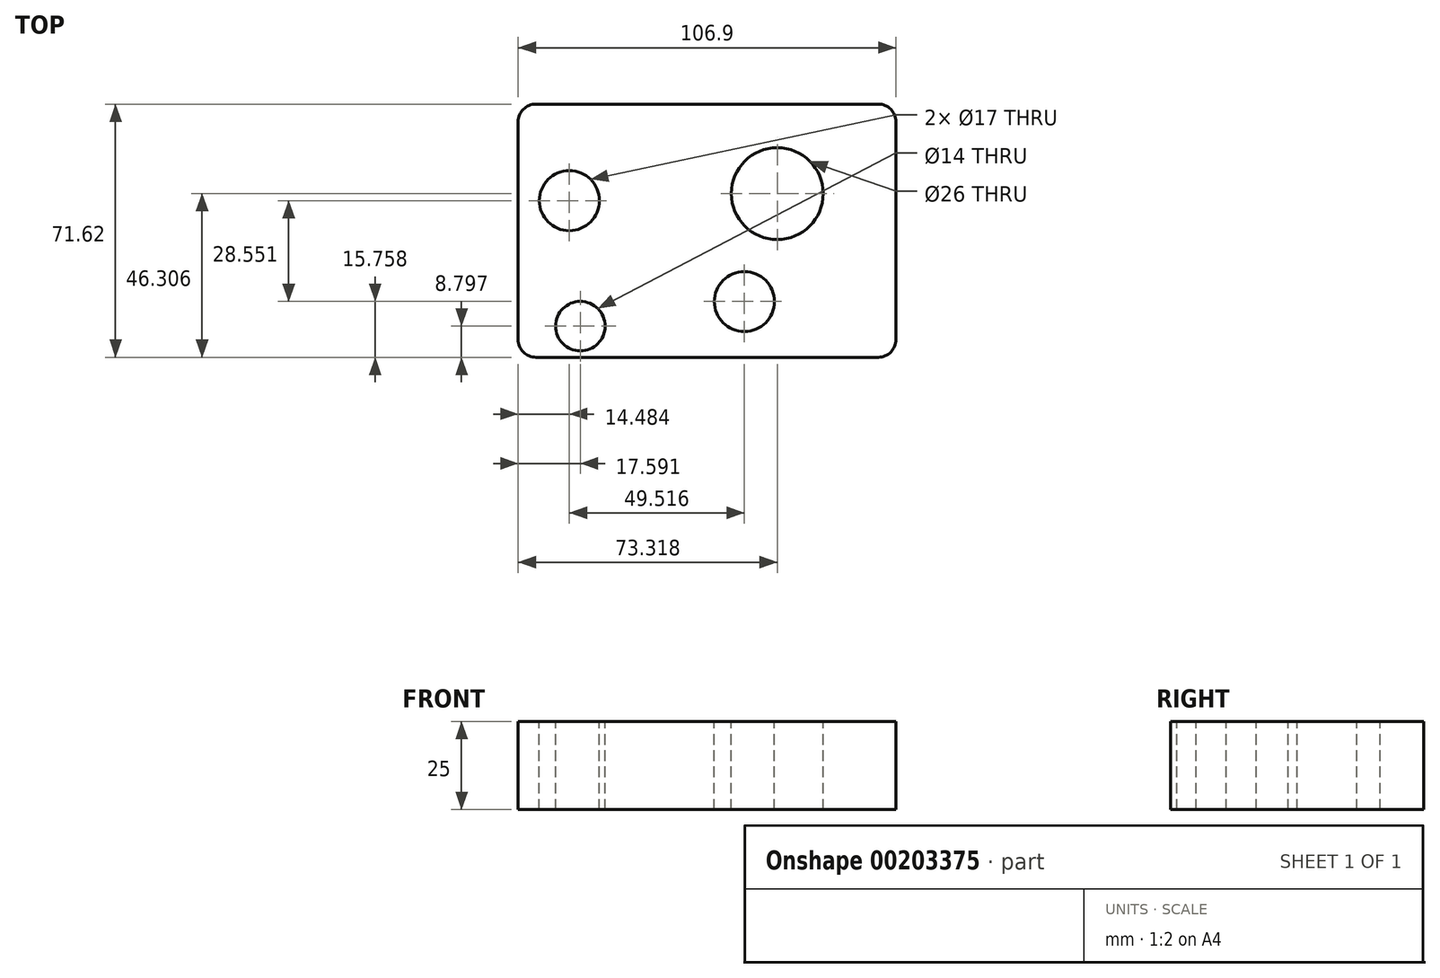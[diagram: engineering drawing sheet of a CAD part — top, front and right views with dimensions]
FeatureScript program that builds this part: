
annotation { "Feature Type Name" : "Feature", "Feature Type Description" : "" }
export const myFeature = defineFeature(function(context is Context, id is Id, definition is map)
    precondition{}
    {
        {
            var Q0;
            Q0=qCreatedBy(makeId("Top.planeOp"),FACE);
            var sketch = newSketch(context, id + "F0", { "sketchPlane" : qUnion([Q0])});
            skLineSegment(sketch, "E0.bottom", {"start": v(-45.31, 0) * mm, "end": v(61.6, 0) * mm});
            skLineSegment(sketch, "E0.top", {"start": v(-45.31, -71.62) * mm, "end": v(61.6, -71.62) * mm});
            skLineSegment(sketch, "E0.left", {"start": v(-45.31, 0) * mm, "end": v(-45.31, -71.62) * mm});
            skLineSegment(sketch, "E0.right", {"start": v(61.6, 0) * mm, "end": v(61.6, -71.62) * mm});
            skSolve(sketch);
        }
        {
            var Q0;
            Q0 = qSketchRegion(id + "F0", true);
            extrude(context, id + "F1", {"entities" : qUnion([Q0]), "depth" : 25 * mm});
        }
        {
            var Q0;
            Q0=makeQuery(id+"F1.opExtrude","SWEPT_EDGE",EDGE,{"disambiguationData":[OSD([sQuery(id+"F0.wireOp",EDGE,"E0.top"),sQuery(id+"F0.wireOp",EDGE,"E0.left")])]});
            var Q1;
            Q1=makeQuery(id+"F1.opExtrude","SWEPT_EDGE",EDGE,{"disambiguationData":[OSD([sQuery(id+"F0.wireOp",EDGE,"E0.top"),sQuery(id+"F0.wireOp",EDGE,"E0.right")])]});
            var Q2;
            Q2=makeQuery(id+"F1.opExtrude","SWEPT_EDGE",EDGE,{"disambiguationData":[OSD([sQuery(id+"F0.wireOp",EDGE,"E0.bottom"),sQuery(id+"F0.wireOp",EDGE,"E0.right")])]});
            var Q3;
            Q3=makeQuery(id+"F1.opExtrude","SWEPT_EDGE",EDGE,{"disambiguationData":[OSD([sQuery(id+"F0.wireOp",EDGE,"E0.bottom"),sQuery(id+"F0.wireOp",EDGE,"E0.left")])]});
            fillet(context, id + "F2", {"entities" : qUnion([Q0, Q1, Q2, Q3]), "radius" : 5 * mm, "tangentPropagation" : true, "allowEdgeOverflow" : false});
        }
        {
            var Q0;
            Q0=makeQuery(id+"F1.opExtrude","CAP_FACE",FACE,{"disambiguationData":[OSD([sQuery(id+"F0.wireOp",EDGE,"E0.bottom"),sQuery(id+"F0.wireOp",EDGE,"E0.top"),sQuery(id+"F0.wireOp",EDGE,"E0.left"),sQuery(id+"F0.wireOp",EDGE,"E0.right")])],"isStart":false});
            var sketch = newSketch(context, id + "F3", { "sketchPlane" : qUnion([Q0])});
            skCircle(sketch, "E1", {"center": v(-27.72, -62.82) * mm, "radius": 7.33 * mm});
            skCircle(sketch, "E2", {"center": v(-30.83, -27.31) * mm, "radius": 8.94 * mm});
            skCircle(sketch, "E3", {"center": v(18.7, -55.86) * mm, "radius": 8.77 * mm});
            skCircle(sketch, "E4", {"center": v(28, -25.31) * mm, "radius": 13.48 * mm});
            skSolve(sketch);
        }
        {
            var Q0;
            Q0=sQuery(id+"F3.wireOp",VERTEX,"E1.center");
            var Q1;
            Q1=makeQuery(id+"F1.opExtrude","SWEPT_BODY",BODY,{"disambiguationData":[OSD([sQuery(id+"F0.wireOp",EDGE,"E0.bottom"),sQuery(id+"F0.wireOp",EDGE,"E0.top"),sQuery(id+"F0.wireOp",EDGE,"E0.left"),sQuery(id+"F0.wireOp",EDGE,"E0.right")])]});
            hole(context, id + "F4", {"style" : HoleStyle.SIMPLE, "endStyle" : HoleEndStyle.THROUGH, "holeDiameter" : 14 * mm, "locations" : qUnion([Q0]), "scope" : qUnion([Q1]), "isTappedThrough" : true});
        }
        {
            var Q0;
            Q0=sQuery(id+"F3.wireOp",VERTEX,"E2.center");
            var Q1;
            Q1=makeQuery(id+"F1.opExtrude","SWEPT_BODY",BODY,{"disambiguationData":[OSD([sQuery(id+"F0.wireOp",EDGE,"E0.bottom"),sQuery(id+"F0.wireOp",EDGE,"E0.top"),sQuery(id+"F0.wireOp",EDGE,"E0.left"),sQuery(id+"F0.wireOp",EDGE,"E0.right")])]});
            hole(context, id + "F5", {"style" : HoleStyle.SIMPLE, "endStyle" : HoleEndStyle.THROUGH, "holeDiameter" : 17 * mm, "locations" : qUnion([Q0]), "scope" : qUnion([Q1]), "isTappedThrough" : true});
        }
        {
            var Q0;
            Q0=sQuery(id+"F3.wireOp",VERTEX,"E3.center");
            var Q1;
            Q1=makeQuery(id+"F1.opExtrude","SWEPT_BODY",BODY,{"disambiguationData":[OSD([sQuery(id+"F0.wireOp",EDGE,"E0.bottom"),sQuery(id+"F0.wireOp",EDGE,"E0.top"),sQuery(id+"F0.wireOp",EDGE,"E0.left"),sQuery(id+"F0.wireOp",EDGE,"E0.right")])]});
            hole(context, id + "F6", {"style" : HoleStyle.SIMPLE, "endStyle" : HoleEndStyle.THROUGH, "holeDiameter" : 17 * mm, "locations" : qUnion([Q0]), "scope" : qUnion([Q1]), "isTappedThrough" : true});
        }
        {
            var Q0;
            Q0=sQuery(id+"F3.wireOp",VERTEX,"E4.center");
            var Q1;
            Q1=makeQuery(id+"F1.opExtrude","SWEPT_BODY",BODY,{"disambiguationData":[OSD([sQuery(id+"F0.wireOp",EDGE,"E0.bottom"),sQuery(id+"F0.wireOp",EDGE,"E0.top"),sQuery(id+"F0.wireOp",EDGE,"E0.left"),sQuery(id+"F0.wireOp",EDGE,"E0.right")])]});
            hole(context, id + "F7", {"style" : HoleStyle.SIMPLE, "endStyle" : HoleEndStyle.THROUGH, "holeDiameter" : 26 * mm, "locations" : qUnion([Q0]), "scope" : qUnion([Q1]), "isTappedThrough" : true});
        }
    });
